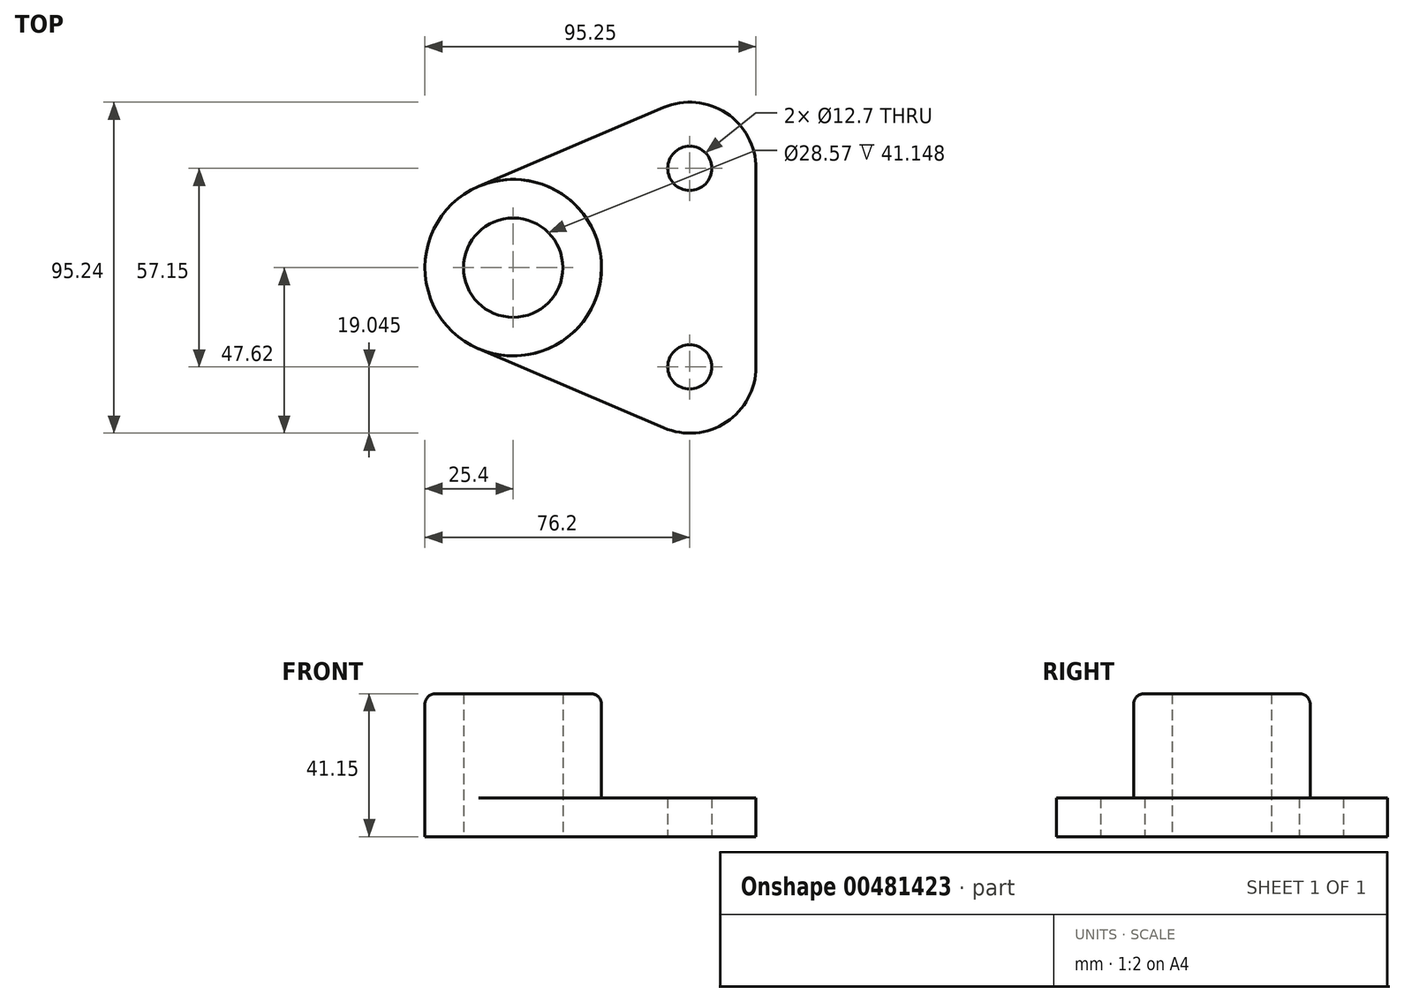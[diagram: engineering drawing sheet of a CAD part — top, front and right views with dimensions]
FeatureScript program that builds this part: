
annotation { "Feature Type Name" : "Feature", "Feature Type Description" : "" }
export const myFeature = defineFeature(function(context is Context, id is Id, definition is map)
    precondition{}
    {
        {
            var Q0;
            Q0=qCreatedBy(makeId("Top.planeOp"),FACE);
            var sketch = newSketch(context, id + "F0", { "sketchPlane" : qUnion([Q0])});
            skCircle(sketch, "E0", {"center": v(-50.8, 0) * mm, "radius": 25.4 * mm});
            skCircle(sketch, "E1", {"center": v(-50.8, 0) * mm, "radius": 14.29 * mm});
            skCircle(sketch, "E2", {"center": v(0, -28.58) * mm, "radius": 6.35 * mm});
            skCircle(sketch, "E3", {"center": v(0, 28.58) * mm, "radius": 6.35 * mm});
            skArc(sketch, "E4", {"start": v(19.05, 28.58) * mm, "mid": v(10.5, 44.47) * mm, "end": v(-7.47, 46.1) * mm});
            skArc(sketch, "E5", {"start": v(-7.47, -46.1) * mm, "mid": v(10.5, -44.47) * mm, "end": v(19.05, -28.58) * mm});
            skLineSegment(sketch, "E6", {"start": v(-60.77, 23.36) * mm, "end": v(-7.47, 46.1) * mm});
            skLineSegment(sketch, "E7", {"start": v(-60.77, -23.36) * mm, "end": v(-7.47, -46.1) * mm});
            skLineSegment(sketch, "E8", {"start": v(19.05, 28.58) * mm, "end": v(19.05, -28.58) * mm});
            skSolve(sketch);
        }
        {
            var Q0;
            Q0=makeQuery(id+"F0.imprint","IMPRINT",FACE,{"disambiguationData":[TD([[makeQuery(id+"F0.imprint","IMPRINT",EDGE,{"derivedFrom":sQuery(id+"F0.wireOp",EDGE,"E1")}),-1.0]])]});
            extrude(context, id + "F1", {"entities" : qUnion([Q0]), "depth" : 41.15 * mm});
        }
        {
            var Q0;
            Q0=makeQuery(id+"F1.opExtrude","CAP_EDGE",EDGE,{"disambiguationData":[OSD([sQuery(id+"F0.wireOp",EDGE,"E0")])],"isStart":false});
            fillet(context, id + "F2", {"entities" : qUnion([Q0]), "radius" : 3.05 * mm, "tangentPropagation" : true, "allowEdgeOverflow" : false});
        }
        {
            var Q0;
            Q0 = qSketchRegion(id + "F0", true);
            extrude(context, id + "F3", {"entities" : qUnion([Q0]), "operationType" : NewBodyOperationType.ADD, "depth" : 11.18 * mm});
        }
    });
